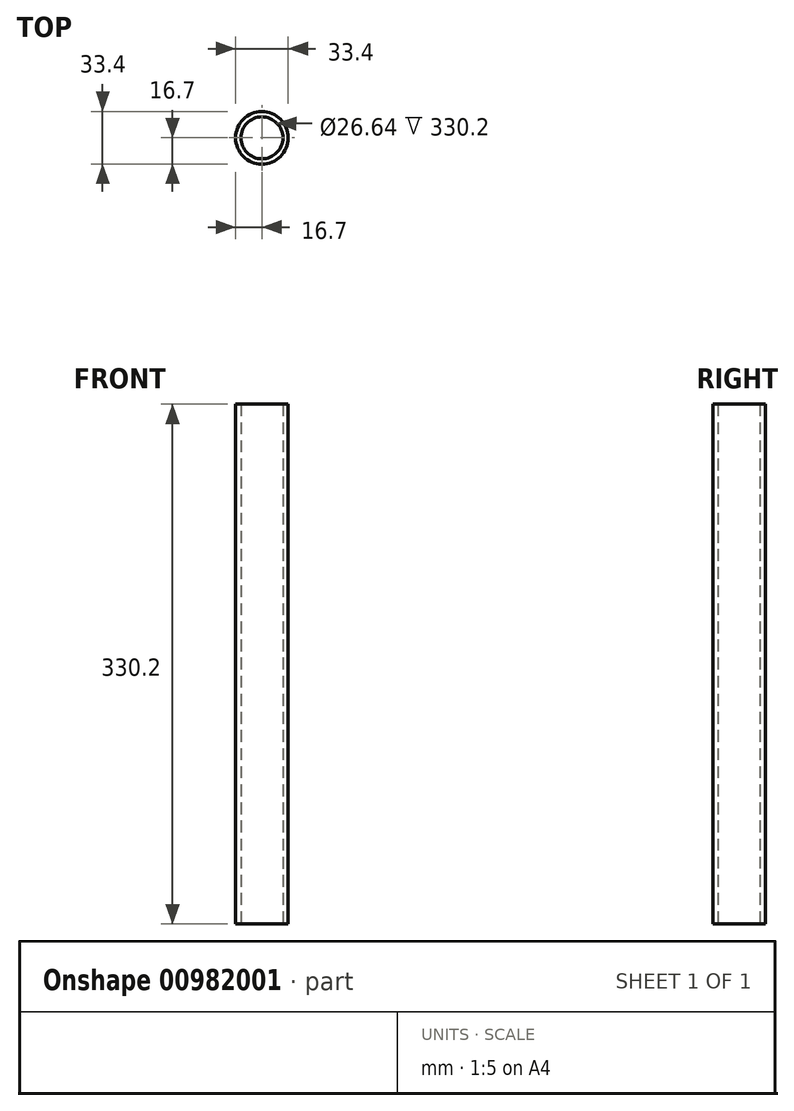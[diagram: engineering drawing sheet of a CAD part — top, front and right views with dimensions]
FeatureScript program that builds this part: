
annotation { "Feature Type Name" : "Feature", "Feature Type Description" : "" }
export const myFeature = defineFeature(function(context is Context, id is Id, definition is map)
    precondition{}
    {
        {
            var Q0;
            Q0=qCreatedBy(makeId("Top.planeOp"),FACE);
            var sketch = newSketch(context, id + "F0", { "sketchPlane" : qUnion([Q0])});
            skCircle(sketch, "E0", {"center": v(0, 0) * mm, "radius": 13.32 * mm});
            skCircle(sketch, "E1", {"center": v(0, 0) * mm, "radius": 16.7 * mm});
            skSolve(sketch);
        }
        {
            var Q0;
            Q0=qSketchRegion(id+"F0",true);
            extrude(context, id + "F1", {"entities" : qUnion([Q0]), "depth" : 330.2 * mm, "offsetDistance" : 25.4 * mm});
        }
    });
